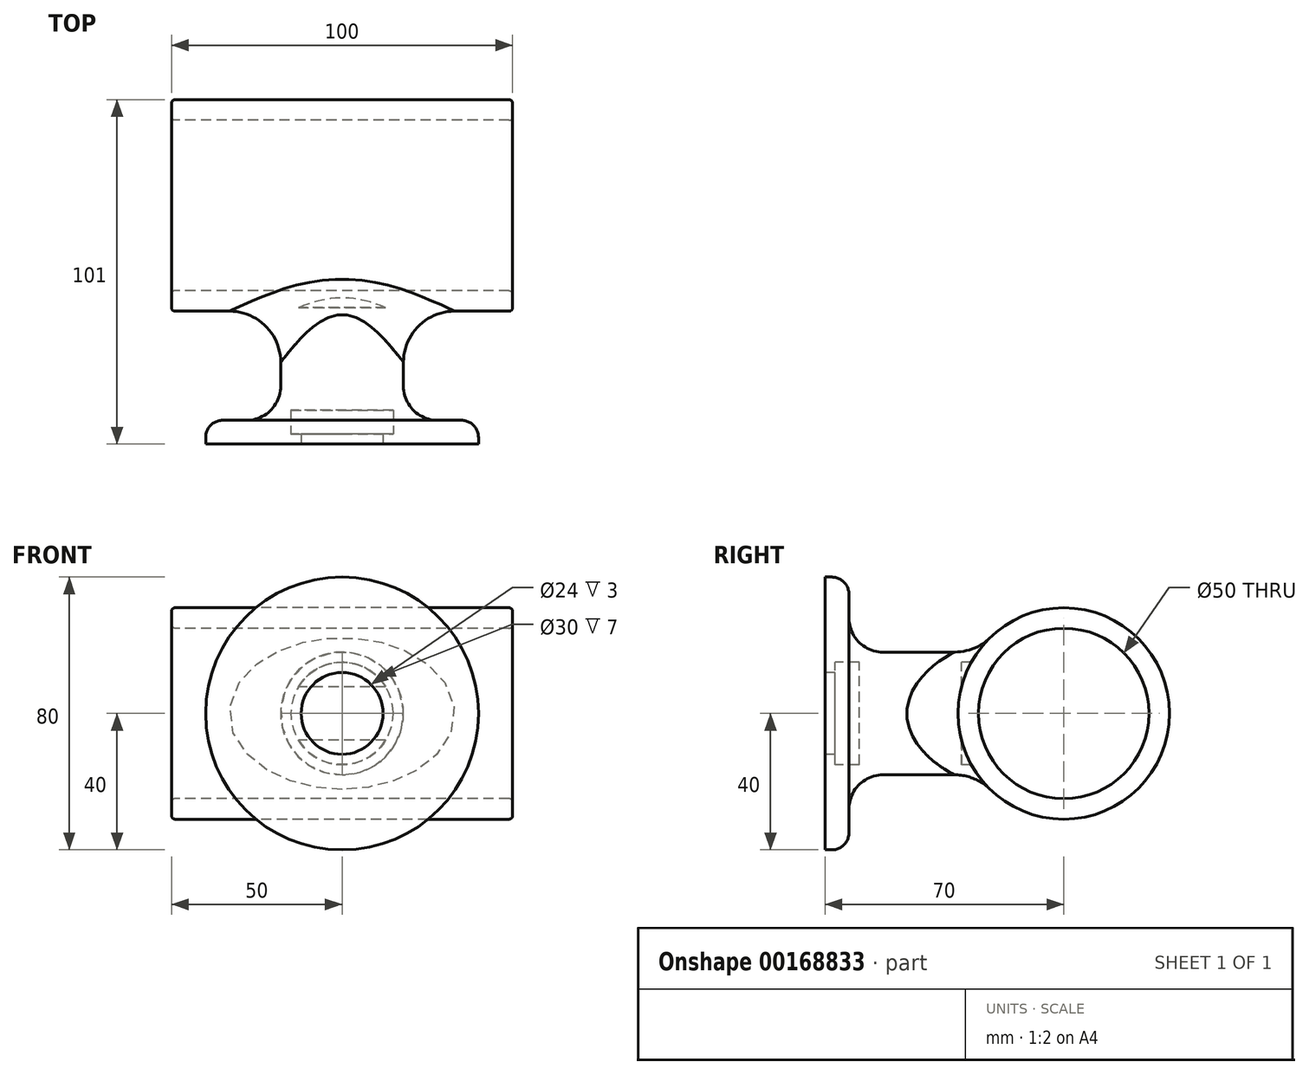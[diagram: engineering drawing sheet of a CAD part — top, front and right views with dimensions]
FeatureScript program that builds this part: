
annotation { "Feature Type Name" : "Feature", "Feature Type Description" : "" }
export const myFeature = defineFeature(function(context is Context, id is Id, definition is map)
    precondition{}
    {
        {
            var Q0;
            Q0=qCreatedBy(makeId("Right.planeOp"),FACE);
            var sketch = newSketch(context, id + "F0", { "sketchPlane" : qUnion([Q0])});
            skLineSegment(sketch, "E0", {"start": v(0, 12) * mm, "end": v(0, 40) * mm});
            skLineSegment(sketch, "E1", {"start": v(0, 40) * mm, "end": v(2, 40) * mm});
            skLineSegment(sketch, "E2", {"start": v(7, 35) * mm, "end": v(7, 28) * mm});
            skLineSegment(sketch, "E3", {"start": v(17, 18) * mm, "end": v(70, 18) * mm});
            skLineSegment(sketch, "E4", {"start": v(70, 18) * mm, "end": v(70, 15) * mm});
            skLineSegment(sketch, "E5", {"start": v(70, 15) * mm, "end": v(40, 15) * mm});
            skLineSegment(sketch, "E6", {"start": v(3, 15) * mm, "end": v(3, 12) * mm});
            skLineSegment(sketch, "E7", {"start": v(3, 12) * mm, "end": v(0, 12) * mm});
            skPoint(sketch, "E8.visualSharp", {"position": v(7, 40) * mm});
            skArc(sketch, "E8.filletArc", {"start": v(7, 35) * mm, "mid": v(5.54, 38.54) * mm, "end": v(2, 40) * mm});
            skPoint(sketch, "E9.visualSharp", {"position": v(7, 18) * mm});
            skArc(sketch, "E9.filletArc", {"start": v(7, 28) * mm, "mid": v(9.93, 20.93) * mm, "end": v(17, 18) * mm});
            skLineSegment(sketch, "E10", {"start": v(10, 15) * mm, "end": v(10, 0) * mm});
            skLineSegment(sketch, "E11", {"start": v(10, 0) * mm, "end": v(40, 0) * mm});
            skLineSegment(sketch, "E12", {"start": v(40, 0) * mm, "end": v(40, 15) * mm});
            skLineSegment(sketch, "E13.trimOffspring", {"start": v(10, 15) * mm, "end": v(3, 15) * mm});
            skSolve(sketch);
        }
        {
            var Q0;
            Q0 = qSketchRegion(id + "F0", true);
            var Q1;
            Q1=sQuery(id+"F0.wireOp",EDGE,"E11");
            revolve(context, id + "F1", {"entities" : qUnion([Q0]), "axis" : qUnion([Q1]), "revolveType" : RevolveType.FULL});
        }
        {
            var Q0;
            Q0=qCreatedBy(makeId("Right.planeOp"),FACE);
            var sketch = newSketch(context, id + "F2", { "sketchPlane" : qUnion([Q0])});
            skCircle(sketch, "E14", {"center": v(70, 0) * mm, "radius": 25 * mm});
            skCircle(sketch, "E15", {"center": v(70, 0) * mm, "radius": 31 * mm});
            skSolve(sketch);
        }
        {
            var Q0;
            Q0 = qSketchRegion(id + "F2", true);
            extrude(context, id + "F3", {"entities" : qUnion([Q0]), "operationType" : NewBodyOperationType.ADD, "endBound" : BoundingType.SYMMETRIC, "depth" : 100 * mm});
        }
        {
            var Q0;
            Q0=makeQuery(id+"F3.opExtrude","CAP_FACE",FACE,{"disambiguationData":[OSD([sQuery(id+"F2.wireOp",EDGE,"E14"),sQuery(id+"F2.wireOp",EDGE,"E15")])],"isStart":false});
            var sketch = newSketch(context, id + "F4", { "sketchPlane" : qUnion([Q0])});
            skCircle(sketch, "E16.0", {"center": v(70, 0) * mm, "radius": 25 * mm});
            skSolve(sketch);
        }
        {
            var Q0;
            Q0 = qSketchRegion(id + "F4", true);
            extrude(context, id + "F5", {"entities" : qUnion([Q0]), "operationType" : NewBodyOperationType.REMOVE, "endBound" : BoundingType.THROUGH_ALL, "oppositeDirection" : true, "depth" : 25 * mm});
        }
        {
            var Q0;
            Q0=makeQuery(id+"F3.boolean.opBoolean","INTERSECT",EDGE,{"derivedFrom":[makeQuery(id+"F1.opRevolve","SWEPT_FACE",FACE,{"disambiguationData":[OSD([sQuery(id+"F0.wireOp",EDGE,"E3")])]}),makeQuery(id+"F3.opExtrude","SWEPT_FACE",FACE,{"disambiguationData":[OSD([sQuery(id+"F2.wireOp",EDGE,"E15")])]})]});
            fillet(context, id + "F6", {"entities" : qUnion([Q0]), "radius" : 15 * mm, "tangentPropagation" : true, "allowEdgeOverflow" : false});
        }
        {
            var Q0;
            Q0=makeQuery(id+"F3.opExtrude","CAP_FACE",FACE,{"disambiguationData":[OSD([sQuery(id+"F2.wireOp",EDGE,"E14"),sQuery(id+"F2.wireOp",EDGE,"E15")])],"isStart":false});
            var Q1;
            Q1=makeQuery(id+"F3.opExtrude","CAP_FACE",FACE,{"disambiguationData":[OSD([sQuery(id+"F2.wireOp",EDGE,"E14"),sQuery(id+"F2.wireOp",EDGE,"E15")])],"isStart":true});
            fillet(context, id + "F7", {"entities" : qUnion([Q0, Q1]), "radius" : 1 * mm, "tangentPropagation" : true, "allowEdgeOverflow" : false});
        }
    });
